# Revit family: Sink-Ligature_Resistant-Whitehall-BestCare-WH3779
name_source: partatom
category: Plumbing Fixtures
units: mm (PartAtom-declared; Revit-internal decimal feet)

## family parameters
Cut with Voids When Loaded = No
Host = Face
OmniClass Number = 23.45.05.14.14
OmniClass Title = Sinks/Lavatories
Part Type = Normal
Room Calculation Point = No
Round Connector Dimension = Use Diameter
Shared = Yes

## types (1)
- WH3779-WH3375-SO
    ADA Compliant = Yes
    Assembly Code = D2010400
    Basin Shape = D Shaped
    CW Connection = Yes
    CWFU = 1.5
    Cold Water Connection Diameter = 1/2"
    Cold Water Connection Height = 20"
    Default Elevation = 34"
    Description = BestCare® Ligature-Resistant Corterra® Solid Surface Double Basin Vanity - ADA Compliant
    Faucet = Faucet-Sensor_Activated-Whitehall-BestCare-WH3375-SO : WH3375-SO
    Finish = Corterra Polymer-Whitehall-OCC11M-Blanco Matte
    Finish - Sink Enclosure = Stailess Steel-Whitehall-Powder Coat White
    HW Connection = Yes
    HWFU = 1.5
    Height = 22 3/4"
    Hot Water Connection Diameter = 1/2"
    IAPMO Compliance = Each standard height Washbasin complies with ANSI, UFAS, and ADA requirements.
    Installation Type = Wall mounted
    Length = 54"
    MC - Mounting Carrier = No
    MXTP- Temperature-Pressure Balancing Mixing Valve (ASSE 1070 Compliant) = No
    Manufacturer = Whitehall Mfg
    Material = Corterra Polymer-Whitehall-OCC11M-Blanco Matte
    Model = WH3779-WH3375-SO
    OCC - Optional Corterra Color - Specify:__ = No
    Operating Pressure = 30 PSI to 100 PSI.
    P-Trap Enclosure Finish (Must Specify) = No
    Product Documentation Link = https://www.whitehallmfg.com
    Product Page URL = https://www.whitehallmfg.com
    URL = https://www.whitehallmfg.com
    Vent Connection = No
    WFU = 2
    WH3775L-SO-Ligature Resistant Faucet 4” Centerset = Yes
    WHST70-12 Tempering Valve With Integral Mounting  Feet Brass Body with 1/2" NPT Connections = No
    Warranty Information = 1 year Limited Warranty
    Waste Connection = Yes
    Waste Connection Height = 23 1/2"
    Water Connection Diameter = 1 1/2"
    Width = 21 3/4"

## geometry (parser evidence)
native form markers: Sweep x5
no freeform markers — native parametric forms only
